# Revit family: S-69
name_source: partatom
category: Pipe Fittings
revit_build: Autodesk Revit 2015 (Build: 20140606_1530(x64)
units: mm (PartAtom-declared; Revit-internal decimal feet)

## types (2) — shared parameters
Aplicación = LAVABO, BIDET
Caudal = 0.4 L/s
Certificados = http://www.jimten.com
Description = SIFON BOTELLA CORTO EXTENSIBLE, SALIDA HORIZONTAL, RACOR CON JUNTA FIX
Manufacturer = Jimten
Material = PP (Blanco)
Model = S-69
Type Comments = FACIL INSTALACION GRACIAS A SU SISTEMA DE JUNTAS INTEGRADAS, TAPON DE REGISTRO INFERIOR
URL = http://www.jimten.com

## per-type parameters (varying)
| type | AlturaMaxima | AlturaMinima | B | DiametroEntrada | DiametroSalida | Entradas | Referencia | Salida |
| S-69_1 1/2" | 220 mm  [stored 0.721785 ft] | 150 mm | 60 mm  [stored 0.19685 ft] | 38 mm | 40 mm  [stored 0.131234 ft] | 1 1/2" ROSCA HEMBRA | 04058 | Ø40 MM (HEMBRA) |
| S-69_1 1/4" | 205 mm  [stored 0.672572 ft] | 140 mm  [stored 0.459318 ft] | 50 mm  [stored 0.164042 ft] | 32 mm  [stored 0.104987 ft] | 32 mm  [stored 0.104987 ft] | 1 1/4" ROSCA HEMBRA | 04016 | Ø32 MM (HEMBRA) |

note: [stored X ft] marks values corroborated as IEEE doubles in the binary element streams (Revit-internal decimal feet)

## geometry (parser evidence)
native form markers: Blend x3
no freeform markers — native parametric forms only
